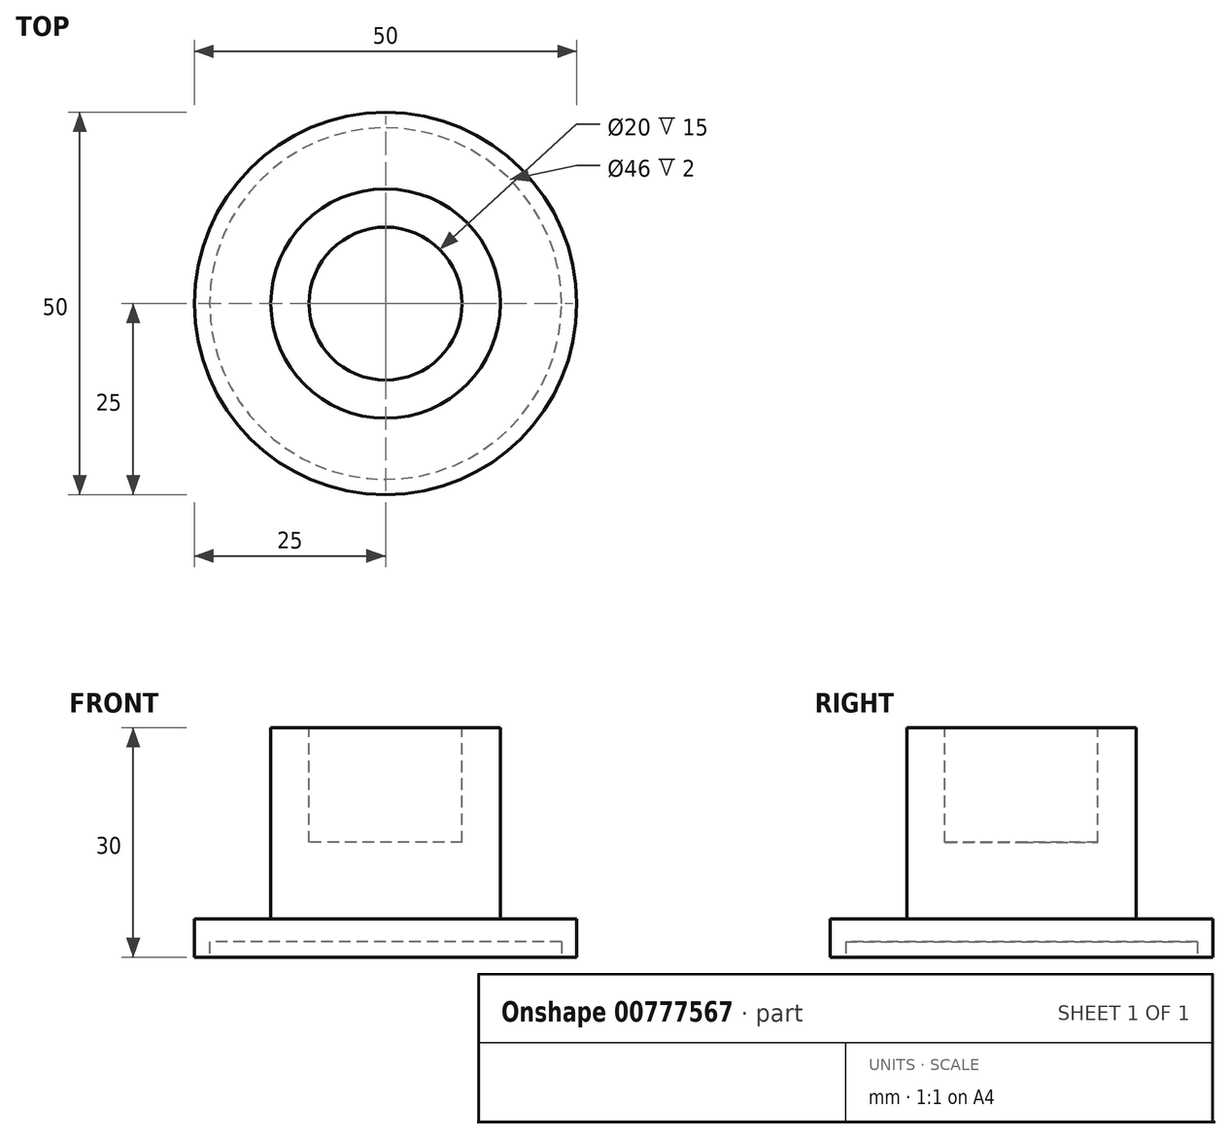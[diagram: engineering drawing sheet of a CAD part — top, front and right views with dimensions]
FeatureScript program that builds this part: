
annotation { "Feature Type Name" : "Feature", "Feature Type Description" : "" }
export const myFeature = defineFeature(function(context is Context, id is Id, definition is map)
    precondition{}
    {
        {
            var Q0;
            Q0=qCreatedBy(makeId("Top.planeOp"),FACE);
            var sketch = newSketch(context, id + "F0", { "sketchPlane" : qUnion([Q0])});
            skCircle(sketch, "E0", {"center": v(0, 0) * mm, "radius": 25 * mm});
            skCircle(sketch, "E1", {"center": v(0, 0) * mm, "radius": 15 * mm});
            skSolve(sketch);
        }
        {
            var Q0;
            Q0 = qSketchRegion(id + "F0", true);
            extrude(context, id + "F1", {"entities" : qUnion([Q0]), "depth" : 5 * mm, "offsetDistance" : 25 * mm});
        }
        {
            var Q0;
            Q0=makeQuery(id+"F0.imprint","IMPRINT",FACE,{"disambiguationData":[TD([[makeQuery(id+"F0.imprint","IMPRINT",EDGE,{"derivedFrom":sQuery(id+"F0.wireOp",EDGE,"E1")}),1.0]])]});
            extrude(context, id + "F2", {"entities" : qUnion([Q0]), "operationType" : NewBodyOperationType.ADD, "depth" : 30 * mm, "offsetDistance" : 25 * mm});
        }
        {
            var Q0;
            Q0=makeQuery(id+"F2.opExtrude","CAP_FACE",FACE,{"disambiguationData":[OSD([sQuery(id+"F0.wireOp",EDGE,"E1")])],"isStart":false});
            var sketch = newSketch(context, id + "F3", { "sketchPlane" : qUnion([Q0])});
            skCircle(sketch, "E2", {"center": v(0, 0) * mm, "radius": 10 * mm});
            skSolve(sketch);
        }
        {
            var Q0;
            Q0 = qSketchRegion(id + "F3", true);
            extrude(context, id + "F4", {"entities" : qUnion([Q0]), "operationType" : NewBodyOperationType.REMOVE, "oppositeDirection" : true, "depth" : 15 * mm, "offsetDistance" : 25 * mm});
        }
        {
            var Q0;
            Q0=makeQuery(id+"F0.imprint","IMPRINT",FACE,{"disambiguationData":[TD([[makeQuery(id+"F0.imprint","IMPRINT",EDGE,{"derivedFrom":sQuery(id+"F0.wireOp",EDGE,"E0")}),1.0]])]});
            var sketch = newSketch(context, id + "F5", { "sketchPlane" : qUnion([Q0])});
            skCircle(sketch, "E3", {"center": v(0, 0) * mm, "radius": 23 * mm});
            skSolve(sketch);
        }
        {
            var Q0;
            Q0 = qSketchRegion(id + "F5", true);
            extrude(context, id + "F6", {"entities" : qUnion([Q0]), "operationType" : NewBodyOperationType.REMOVE, "depth" : 2 * mm, "offsetDistance" : 25 * mm});
        }
    });
